# Revit family: Gira_125800
name_source: partatom
category: Electrical Fixtures
revit_build: Autodesk Revit 2017 (Build: 20160225_1515(x64)
units: mm (PartAtom-declared; Revit-internal decimal feet)

## family parameters
Cut with Voids When Loaded = No
Host = Face
Maintain Annotation Orientation = Yes
Part Type = Normal
Room Calculation Point = No
Round Connector Dimension = Use Diameter
Shared = No

## types (1)
- Built-in spkeaker Door communication
    Available = No
    BIM (1) = https://media.stage.bim.site und Tasten.rfa?public/gira/36a6b08/Türstation_Schalten und Tasten.rfa
    Category = Mounting accessories for door communication
    Data sheet (1) = https://katalog.gira.de
    Default Elevation = 1219 mm
    Description = B-i spk. Door,Built-in speaker,,,Features:,- Built-in speaker for mounting in letterbox systems, voice compartments, door-side installations or front plates. ,- Up to eight mechanical bell buttons can be connected to the screw terminals provided.,- Signal transmission and power supply of speaker via reverse-polarity-protected and short-circuit-proof 2-wire bus.,- Compact size.,- Weather-resistant speaker.,- High-quality electret microphone.,- Alternating current polling of the bell button connections to prevent oxidation on the button contacts.,- Securing of connection terminals against incorrect connection.,- Up to eight mechanical bell buttons can be connected.,- Colour camera for door station can be connected.,- Speakerphone function (voice-controlled talk-back with echo and background noise suppression).,- Adjustable voice volume.,- One-man start-up with easy start-up procedure.,- Audible acknowledgement signal when a call button is pressed.,,Notes :,- This component enables door communication systems with up to 140 audio devices to be set up (e.g. 1 x built-in speaker, 11 x add-on modules for built-in speakers, 136 x surface-mounted home stations).,- The video control device is required if the system is extended with a colour camera.
    GTIN = 4010337258001
    HAN = 125800
    HeinzeBIM = https://bimportal.heinze.de
    Manufacturer = Gira
    Manufacturer URL = https://www.gira.de
    Material = Other
    Name = Built-in spkeaker Door communication
    Suitable for = Outdoor station
    URL = http://katalog.gira.de

## geometry (parser evidence)
native form markers: Sweep x3
no freeform markers — native parametric forms only
